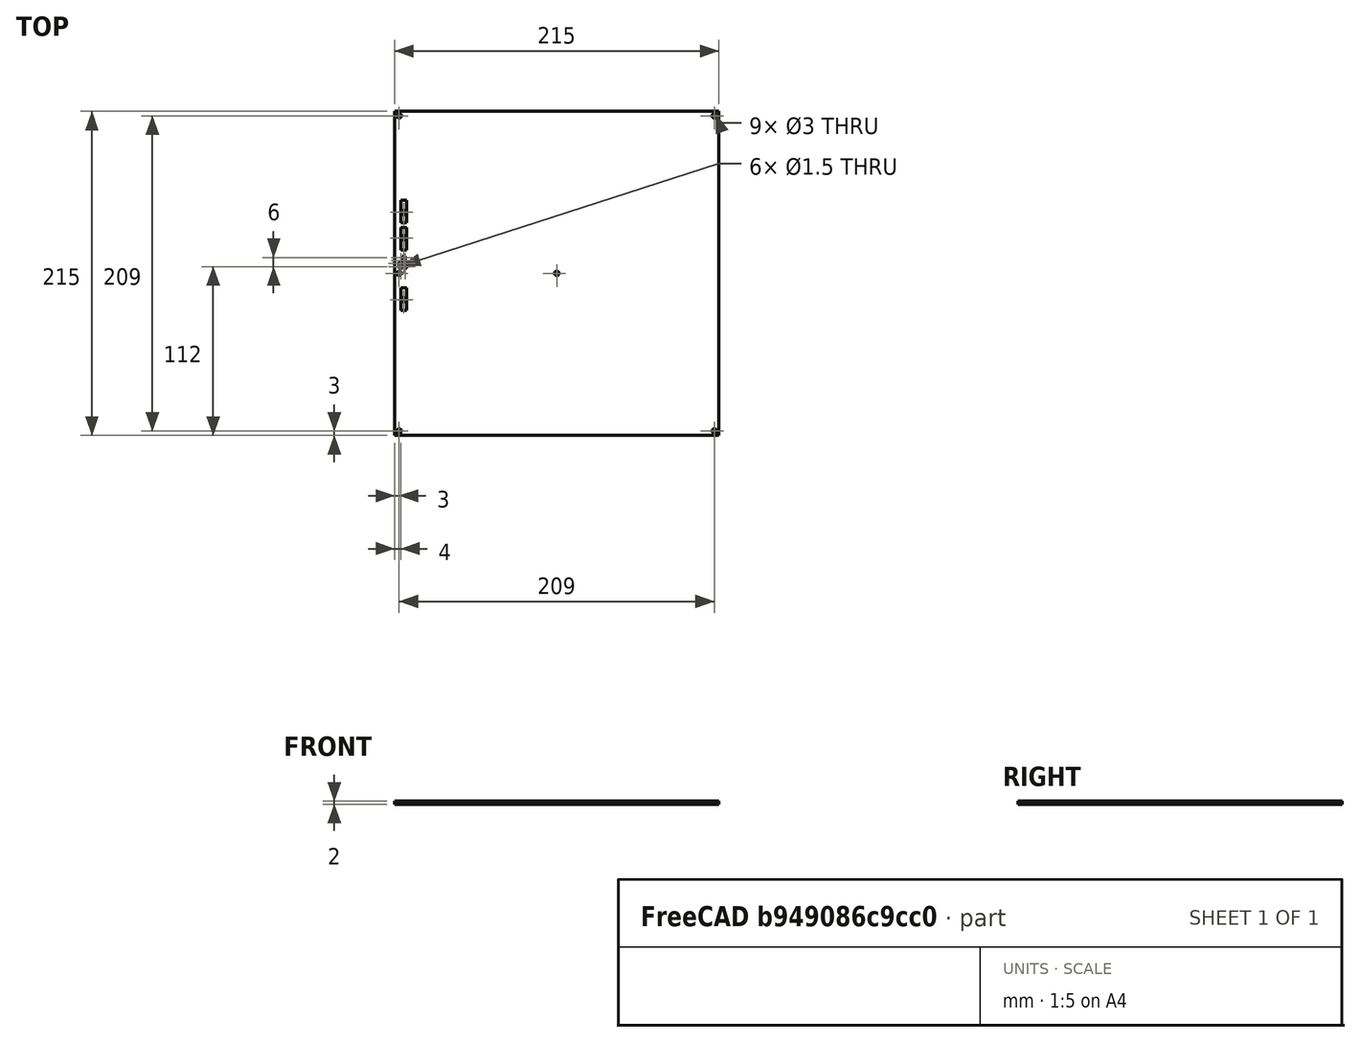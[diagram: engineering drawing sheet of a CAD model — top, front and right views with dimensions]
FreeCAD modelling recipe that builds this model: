
FCSTD DOCUMENT  (FreeCAD 0.14R3700 (Git))
Label: MK2 Heatbed Mockup
License: CC-BY 3.0
LicenseURL: http://creativecommons.org/licenses/by/3.0/
objects: Part::Cut×21, Part::Cylinder×15, Part::Box×7
note: 43 computed .brp shape members not serialized (recipe doc carries the construction recipe); baked Part::Feature solids carry a one-line shape summary decoded from their .brp

FEATURE [Part::Box] Box  label="Cube"
  Height = 2
  Length = 215
  Width = 215
FEATURE [Part::Cylinder] Cylinder
  Angle = 360
  Height = 10
  Placement = pos=(212,3,0) rot=(0,0,1;0rad)
  Radius = 1.5
FEATURE [Part::Cylinder] Cylinder001
  Angle = 360
  Height = 10
  Placement = pos=(3,3,0) rot=(0,0,1;0rad)
  Radius = 1.5
FEATURE [Part::Cylinder] Cylinder002
  Angle = 360
  Height = 10
  Placement = pos=(212,212,0) rot=(0,0,1;0rad)
  Radius = 1.5
FEATURE [Part::Cylinder] Cylinder003
  Angle = 360
  Height = 10
  Placement = pos=(3,212,0) rot=(0,0,1;0rad)
  Radius = 1.5
FEATURE [Part::Cylinder] Cylinder004
  Angle = 360
  Height = 10
  Placement = pos=(107.5,107.5,0) rot=(0,0,1;0rad)
  Radius = 1.5
FEATURE [Part::Cylinder] Cylinder005
  Angle = 360
  Height = 10
  Placement = pos=(6,90,0) rot=(0,0,1;0rad)
  Radius = 1.5
FEATURE [Part::Cylinder] Cylinder006
  Angle = 360
  Height = 10
  Placement = pos=(3,107.5,0) rot=(0,0,1;0rad)
  Radius = 1.5
FEATURE [Part::Cylinder] Cylinder007
  Angle = 360
  Height = 10
  Placement = pos=(6,131,0) rot=(0,0,1;0rad)
  Radius = 1.5
FEATURE [Part::Cylinder] Cylinder008
  Angle = 360
  Height = 10
  Placement = pos=(6,148,0) rot=(0,0,1;0rad)
  Radius = 1.5
FEATURE [Part::Cylinder] Cylinder009
  Angle = 360
  Height = 10
  Placement = pos=(4,112,0) rot=(0,0,1;0rad)
  Radius = 0.75
FEATURE [Part::Cut] Cut
  Base = -> Box
  Tool = -> Cylinder001
FEATURE [Part::Cut] Cut001
  Base = -> Cut
  Tool = -> Cylinder
FEATURE [Part::Cut] Cut002
  Base = -> Cut001
  Tool = -> Cylinder002
FEATURE [Part::Cut] Cut003
  Base = -> Cut002
  Tool = -> Cylinder004
FEATURE [Part::Cut] Cut004
  Base = -> Cut003
  Tool = -> Cylinder003
FEATURE [Part::Cut] Cut005
  Base = -> Cut004
  Tool = -> Cylinder005
FEATURE [Part::Cut] Cut006
  Base = -> Cut005
  Tool = -> Cylinder008
FEATURE [Part::Cut] Cut007
  Base = -> Cut006
  Tool = -> Cylinder007
FEATURE [Part::Cut] Cut008
  Base = -> Cut007
  Tool = -> Cylinder006
FEATURE [Part::Cylinder] Cylinder010
  Angle = 360
  Height = 10
  Placement = pos=(4,114,0) rot=(0,0,1;0rad)
  Radius = 0.75
FEATURE [Part::Cylinder] Cylinder011
  Angle = 360
  Height = 10
  Placement = pos=(6,116,0) rot=(0,0,1;0rad)
  Radius = 0.75
FEATURE [Part::Cylinder] Cylinder012
  Angle = 360
  Height = 10
  Placement = pos=(6,118,0) rot=(0,0,1;0rad)
  Radius = 0.75
FEATURE [Part::Cylinder] Cylinder013
  Angle = 360
  Height = 10
  Placement = pos=(7,112,0) rot=(0,0,1;0rad)
  Radius = 0.75
FEATURE [Part::Cylinder] Cylinder014
  Angle = 360
  Height = 10
  Placement = pos=(7,114,0) rot=(0,0,1;0rad)
  Radius = 0.75
FEATURE [Part::Cut] Cut009
  Base = -> Cut008
  Tool = -> Cylinder009
FEATURE [Part::Cut] Cut010
  Base = -> Cut009
  Tool = -> Cylinder013
FEATURE [Part::Cut] Cut011
  Base = -> Cut010
  Tool = -> Cylinder014
FEATURE [Part::Cut] Cut012
  Base = -> Cut011
  Tool = -> Cylinder010
FEATURE [Part::Cut] Cut013
  Base = -> Cut012
  Tool = -> Cylinder011
FEATURE [Part::Cut] Cut014
  Base = -> Cut013
  Tool = -> Cylinder012
FEATURE [Part::Box] Box001  label="Cube001"
  Height = 0.5
  Length = 4
  Placement = pos=(4,83,1.75) rot=(0,0,1;0rad)
  Width = 15
FEATURE [Part::Box] Box002  label="Cube002"
  Height = 0.5
  Length = 4
  Placement = pos=(4,123,1.75) rot=(0,0,1;0rad)
  Width = 15
FEATURE [Part::Box] Box003  label="Cube003"
  Height = 0.5
  Length = 4
  Placement = pos=(4,141,1.75) rot=(0,0,1;0rad)
  Width = 15
FEATURE [Part::Box] Box004  label="Cube004"
  Height = 0.5
  Length = 2
  Placement = pos=(3,111,1.75) rot=(0,0,1;0rad)
  Width = 4
FEATURE [Part::Cut] Cut015
  Base = -> Cut014
  Tool = -> Box001
FEATURE [Part::Cut] Cut016
  Base = -> Cut015
  Tool = -> Box002
FEATURE [Part::Cut] Cut017
  Base = -> Cut016
  Tool = -> Box003
FEATURE [Part::Box] Box005  label="Cube005"
  Height = 0.5
  Length = 2
  Placement = pos=(6,111,1.75) rot=(0,0,1;0rad)
  Width = 4
FEATURE [Part::Box] Box006  label="Cube006"
  Height = 0.5
  Length = 2
  Placement = pos=(5,115,1.75) rot=(0,0,1;0rad)
  Width = 4
FEATURE [Part::Cut] Cut018
  Base = -> Cut017
  Tool = -> Box004
FEATURE [Part::Cut] Cut019
  Base = -> Cut018
  Tool = -> Box006
FEATURE [Part::Cut] Cut020
  Base = -> Cut019
  Tool = -> Box005
